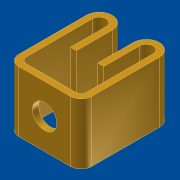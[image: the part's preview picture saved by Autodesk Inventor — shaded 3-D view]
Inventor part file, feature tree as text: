
AUTODESK INVENTOR PART (.ipt)
format: ipt  version: unknown  size: 213,504 bytes
history: native  units: mm
features: sketch x2, extrude x1, mirror x1, hole x1
ambient origin geometry x8: Origin, YZ Plane, XZ Plane, XY Plane, X Axis, Y Axis, Z Axis, Center Point
feature tree (5):
  extrude  "Extrusion1"  [1 undecoded]
  mirror  "Mirror1"
  hole  "Hole1"  [1 undecoded]
  sketch  "Sketch1"  dims[d0=10.0mm d1=0.0mm]
  sketch  "Sketch2"  dims[d2=4.0mm d3=6.0mm d4=4.0mm d5=2.0mm d6=90.0deg d7=2.0mm d8=20.594885mm]
note: 2 required parameter values undecoded (feature->parameter linkage not recoverable at this tier; creation-order binding heuristic only, values carry confidence <= 0.55)
